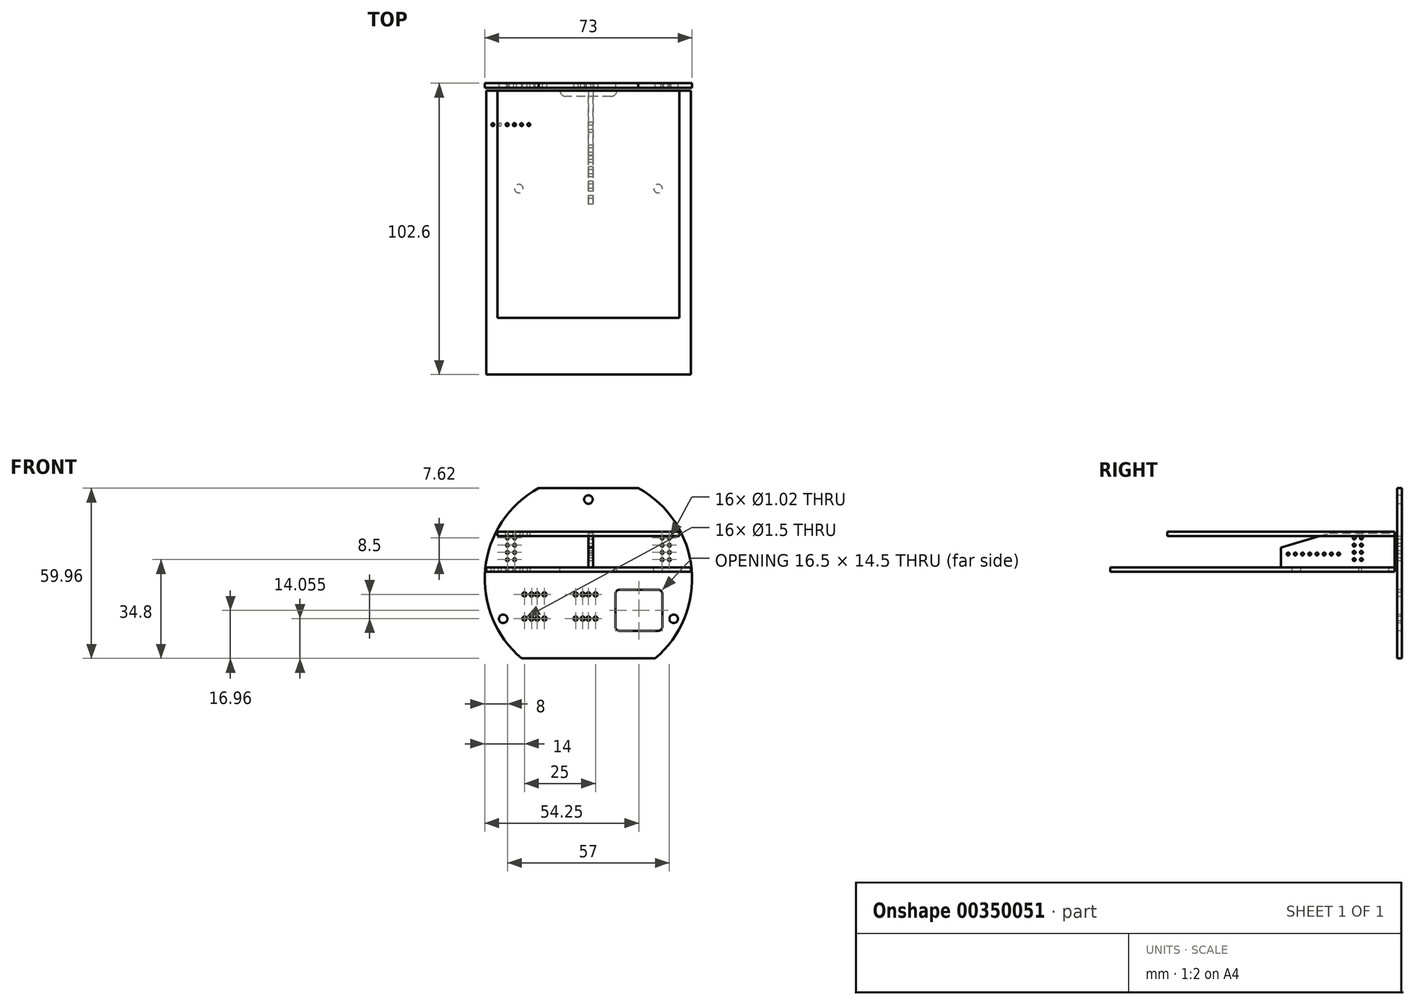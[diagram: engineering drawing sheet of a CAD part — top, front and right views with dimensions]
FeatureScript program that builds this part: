
annotation { "Feature Type Name" : "Feature", "Feature Type Description" : "" }
export const myFeature = defineFeature(function(context is Context, id is Id, definition is map)
    precondition{}
    {
        {
            var Q0;
            Q0=qCreatedBy(makeId("Front.planeOp"),FACE);
            var sketch = newSketch(context, id + "F0", { "sketchPlane" : qUnion([Q0])});
            skCircle(sketch, "E0", {"center": v(0, 0) * mm, "radius": 36.5 * mm});
            skLineSegment(sketch, "E1", {"start": v(-23.46, -27.96) * mm, "end": v(23.46, -27.96) * mm});
            skLineSegment(sketch, "E2", {"start": v(0, 0) * mm, "end": v(-23.46, -27.96) * mm, "construction": true});
            skLineSegment(sketch, "E3", {"start": v(0, 0) * mm, "end": v(23.46, -27.96) * mm, "construction": true});
            skLineSegment(sketch, "E4", {"start": v(17.56, 32) * mm, "end": v(-17.56, 32) * mm});
            skSolve(sketch);
        }
        {
            var Q0;
            {var subQ0=sQuery(id+"F0.wireOp",EDGE,"E1");Q0=makeQuery(id+"F0.imprint","IMPRINT",FACE,{"disambiguationData":[TD([[makeQuery(id+"F0.imprint","IMPRINT",EDGE,{"derivedFrom":subQ0}),1.0]])]});}
            extrude(context, id + "F1", {"entities" : qUnion([Q0]), "depth" : 1.6 * mm});
        }
        {
            var Q0;
            Q0=makeQuery(id+"F1.opExtrude","CAP_FACE",FACE,{"disambiguationData":[OSD([sQuery(id+"F0.wireOp",EDGE,"E0"),sQuery(id+"F0.wireOp",EDGE,"E1")])],"isStart":false});
            var sketch = newSketch(context, id + "F2", { "sketchPlane" : qUnion([Q0])});
            skCircle(sketch, "E5", {"center": v(28.5, 14.46) * mm, "radius": 0.5 * mm});
            skCircle(sketch, "E6.0.1.0", {"center": v(28.5, 11.92) * mm, "radius": 0.5 * mm});
            skCircle(sketch, "E6.0.2.0", {"center": v(28.5, 9.38) * mm, "radius": 0.5 * mm});
            skCircle(sketch, "E6.0.3.0", {"center": v(28.5, 6.84) * mm, "radius": 0.5 * mm});
            skCircle(sketch, "E6.1.0.0", {"center": v(25.96, 14.46) * mm, "radius": 0.5 * mm});
            skCircle(sketch, "E6.1.1.0", {"center": v(25.96, 11.92) * mm, "radius": 0.5 * mm});
            skCircle(sketch, "E6.1.2.0", {"center": v(25.96, 9.38) * mm, "radius": 0.5 * mm});
            skCircle(sketch, "E6.1.3.0", {"center": v(25.96, 6.84) * mm, "radius": 0.5 * mm});
            skLineSegment(sketch, "E6.direction1", {"start": v(28.5, 14.46) * mm, "end": v(25.96, 14.46) * mm, "construction": true});
            skLineSegment(sketch, "E6.direction2", {"start": v(28.5, 14.46) * mm, "end": v(28.5, 11.92) * mm, "construction": true});
            skLineSegment(sketch, "E7.bottom", {"start": v(24.5, -3.75) * mm, "end": v(11, -3.75) * mm});
            skLineSegment(sketch, "E7.top", {"start": v(24.5, -18.25) * mm, "end": v(11, -18.25) * mm});
            skLineSegment(sketch, "E7.left", {"start": v(26, -5.25) * mm, "end": v(26, -16.75) * mm});
            skLineSegment(sketch, "E7.right", {"start": v(9.5, -5.25) * mm, "end": v(9.5, -16.75) * mm});
            skPoint(sketch, "E7.middle", {"position": v(17.75, -11) * mm});
            skPoint(sketch, "E8.visualSharp", {"position": v(9.5, -3.75) * mm});
            skArc(sketch, "E8.filletArc", {"start": v(11, -3.75) * mm, "mid": v(9.94, -4.19) * mm, "end": v(9.5, -5.25) * mm});
            skPoint(sketch, "E9.visualSharp", {"position": v(26, -3.75) * mm});
            skArc(sketch, "E9.filletArc", {"start": v(26, -5.25) * mm, "mid": v(25.56, -4.19) * mm, "end": v(24.5, -3.75) * mm});
            skPoint(sketch, "E10.visualSharp", {"position": v(26, -18.25) * mm});
            skArc(sketch, "E10.filletArc", {"start": v(24.5, -18.25) * mm, "mid": v(25.56, -17.81) * mm, "end": v(26, -16.75) * mm});
            skPoint(sketch, "E11.visualSharp", {"position": v(9.5, -18.25) * mm});
            skArc(sketch, "E11.filletArc", {"start": v(9.5, -16.75) * mm, "mid": v(9.94, -17.81) * mm, "end": v(11, -18.25) * mm});
            skCircle(sketch, "E12", {"center": v(-22.5, -5.4) * mm, "radius": 0.75 * mm});
            skCircle(sketch, "E13", {"center": v(-20, -5.4) * mm, "radius": 0.75 * mm});
            skCircle(sketch, "E14", {"center": v(-18, -5.4) * mm, "radius": 0.75 * mm});
            skCircle(sketch, "E15", {"center": v(-15.5, -5.4) * mm, "radius": 0.75 * mm});
            skCircle(sketch, "E16.0.1.0", {"center": v(-22.5, -13.9) * mm, "radius": 0.75 * mm});
            skCircle(sketch, "E16.0.1.1", {"center": v(-20, -13.9) * mm, "radius": 0.75 * mm});
            skCircle(sketch, "E16.0.1.2", {"center": v(-18, -13.9) * mm, "radius": 0.75 * mm});
            skCircle(sketch, "E16.0.1.3", {"center": v(-15.5, -13.9) * mm, "radius": 0.75 * mm});
            skCircle(sketch, "E16.1.0.0", {"center": v(-4.5, -5.4) * mm, "radius": 0.75 * mm});
            skCircle(sketch, "E16.1.0.1", {"center": v(-2, -5.4) * mm, "radius": 0.75 * mm});
            skCircle(sketch, "E16.1.0.2", {"center": v(0, -5.4) * mm, "radius": 0.75 * mm});
            skCircle(sketch, "E16.1.0.3", {"center": v(2.5, -5.4) * mm, "radius": 0.75 * mm});
            skCircle(sketch, "E16.1.1.0", {"center": v(-4.5, -13.9) * mm, "radius": 0.75 * mm});
            skCircle(sketch, "E16.1.1.1", {"center": v(-2, -13.9) * mm, "radius": 0.75 * mm});
            skCircle(sketch, "E16.1.1.2", {"center": v(0, -13.9) * mm, "radius": 0.75 * mm});
            skCircle(sketch, "E16.1.1.3", {"center": v(2.5, -13.9) * mm, "radius": 0.75 * mm});
            skLineSegment(sketch, "E16.direction1", {"start": v(-22.5, -5.4) * mm, "end": v(-4.5, -5.4) * mm, "construction": true});
            skLineSegment(sketch, "E16.direction2", {"start": v(-22.5, -5.4) * mm, "end": v(-22.5, -13.9) * mm, "construction": true});
            skPoint(sketch, "E17", {"position": v(-36.5, 0) * mm});
            skLineSegment(sketch, "E18", {"start": v(0, 0) * mm, "end": v(0, 16.77) * mm, "construction": true});
            skCircle(sketch, "E19.MirrorC", {"center": v(-25.96, 6.84) * mm, "radius": 0.5 * mm});
            skCircle(sketch, "E20.MirrorC", {"center": v(-25.96, 9.38) * mm, "radius": 0.5 * mm});
            skCircle(sketch, "E21.MirrorC", {"center": v(-25.96, 11.92) * mm, "radius": 0.5 * mm});
            skCircle(sketch, "E22.MirrorC", {"center": v(-25.96, 14.46) * mm, "radius": 0.5 * mm});
            skCircle(sketch, "E23.MirrorC", {"center": v(-28.5, 14.46) * mm, "radius": 0.5 * mm});
            skCircle(sketch, "E24.MirrorC", {"center": v(-28.5, 11.92) * mm, "radius": 0.5 * mm});
            skCircle(sketch, "E25.MirrorC", {"center": v(-28.5, 9.38) * mm, "radius": 0.5 * mm});
            skCircle(sketch, "E26.MirrorC", {"center": v(-28.5, 6.84) * mm, "radius": 0.5 * mm});
            skLineSegment(sketch, "E27", {"start": v(28.5, 6.84) * mm, "end": v(25.96, 14.46) * mm, "construction": true});
            skLineSegment(sketch, "E28.bottom", {"start": v(29.73, 15.98) * mm, "end": v(24.73, 15.98) * mm, "construction": true});
            skLineSegment(sketch, "E28.top", {"start": v(29.73, 5.32) * mm, "end": v(24.73, 5.32) * mm, "construction": true});
            skLineSegment(sketch, "E28.left", {"start": v(29.73, 15.98) * mm, "end": v(29.73, 5.32) * mm, "construction": true});
            skLineSegment(sketch, "E28.right", {"start": v(24.73, 15.98) * mm, "end": v(24.73, 5.32) * mm, "construction": true});
            skPoint(sketch, "E28.middle", {"position": v(27.23, 10.65) * mm});
            skLineSegment(sketch, "E29", {"start": v(31.33, 17.45) * mm, "end": v(31.33, 3.87) * mm, "construction": true});
            skCircle(sketch, "E30", {"center": v(0, 28) * mm, "radius": 1.5 * mm});
            skCircle(sketch, "E31", {"center": v(-30, -14) * mm, "radius": 1.5 * mm});
            skCircle(sketch, "E32.MirrorC", {"center": v(30, -14) * mm, "radius": 1.5 * mm});
            skSolve(sketch);
        }
        {
            var Q0;
            Q0=qSketchRegion(id+"F2",true);
            extrude(context, id + "F3", {"entities" : qUnion([Q0]), "operationType" : NewBodyOperationType.REMOVE, "oppositeDirection" : true, "depth" : 25 * mm});
        }
        {
            var Q0;
            Q0=makeQuery(id+"F1.opExtrude","CAP_FACE",FACE,{"disambiguationData":[OSD([sQuery(id+"F0.wireOp",EDGE,"E0"),sQuery(id+"F0.wireOp",EDGE,"E1")])],"isStart":false});
            cPlane(context, id + "F4", {"entities" : qUnion([Q0]), "cplaneType" : CPlaneType.OFFSET, "offset" : 1 * mm, "width" : 150 * mm, "height" : 150 * mm});
        }
        {
            var Q0;
            Q0=qCreatedBy(id+"F4.planeOp",FACE);
            var sketch = newSketch(context, id + "F5", { "sketchPlane" : qUnion([Q0])});
            skLineSegment(sketch, "E33.bottom", {"start": v(-36, 4.12) * mm, "end": v(36, 4.12) * mm});
            skLineSegment(sketch, "E33.top", {"start": v(-36, 2.52) * mm, "end": v(36, 2.52) * mm});
            skLineSegment(sketch, "E33.left", {"start": v(-36, 4.12) * mm, "end": v(-36, 2.52) * mm});
            skLineSegment(sketch, "E33.right", {"start": v(36, 4.12) * mm, "end": v(36, 2.52) * mm});
            skPoint(sketch, "E33.middle", {"position": v(0, 3.32) * mm});
            skCircle(sketch, "E34", {"center": v(0, 0) * mm, "radius": 36.5 * mm, "construction": true});
            skSolve(sketch);
        }
        {
            var Q0;
            Q0=qSketchRegion(id+"F5",true);
            extrude(context, id + "F6", {"entities" : qUnion([Q0]), "depth" : 100 * mm});
        }
        {
            var Q0;
            Q0=makeQuery(id+"F6.opExtrude","SWEPT_FACE",FACE,{"disambiguationData":[OSD([sQuery(id+"F5.wireOp",EDGE,"E33.bottom")])]});
            var sketch = newSketch(context, id + "F7", { "sketchPlane" : qUnion([Q0])});
            skCircle(sketch, "E35", {"center": v(24.5, -37.1) * mm, "radius": 1.5 * mm});
            skLineSegment(sketch, "E36", {"start": v(0, 0) * mm, "end": v(0, -31.2) * mm, "construction": true});
            skPoint(sketch, "E36.endSnap0", {"position": v(0, -2.6) * mm});
            skPoint(sketch, "E37", {"position": v(0, -102.6) * mm});
            skLineSegment(sketch, "E38.bottom", {"start": v(10, -2.6) * mm, "end": v(-10, -2.6) * mm});
            skLineSegment(sketch, "E38.top", {"start": v(8, -4.6) * mm, "end": v(-8, -4.6) * mm});
            skLineSegment(sketch, "E38.left", {"start": v(10, -2.6) * mm, "end": v(10, -2.6) * mm});
            skLineSegment(sketch, "E38.right", {"start": v(-10, -2.6) * mm, "end": v(-10, -2.6) * mm});
            skPoint(sketch, "E38.middle", {"position": v(0, -3.6) * mm});
            skPoint(sketch, "E39.visualSharp", {"position": v(10, -4.6) * mm});
            skArc(sketch, "E39.filletArc", {"start": v(8, -4.6) * mm, "mid": v(9.41, -4.01) * mm, "end": v(10, -2.6) * mm});
            skPoint(sketch, "E40.visualSharp", {"position": v(-10, -4.6) * mm});
            skArc(sketch, "E40.filletArc", {"start": v(-10, -2.6) * mm, "mid": v(-9.41, -4.01) * mm, "end": v(-8, -4.6) * mm});
            skCircle(sketch, "E41.MirrorC", {"center": v(-24.5, -37.1) * mm, "radius": 1.5 * mm});
            skCircle(sketch, "E42", {"center": v(-26, -14.57) * mm, "radius": 0.5 * mm});
            skCircle(sketch, "E43.1.0.0", {"center": v(-28.54, -14.57) * mm, "radius": 0.5 * mm});
            skCircle(sketch, "E43.2.0.0", {"center": v(-31.08, -14.57) * mm, "radius": 0.5 * mm});
            skCircle(sketch, "E43.3.0.0", {"center": v(-33.62, -14.57) * mm, "radius": 0.5 * mm});
            skLineSegment(sketch, "E43.direction1", {"start": v(-26, -14.57) * mm, "end": v(-28.54, -14.57) * mm, "construction": true});
            skSolve(sketch);
        }
        {
            var Q0;
            Q0=qSketchRegion(id+"F7",true);
            extrude(context, id + "F8", {"entities" : qUnion([Q0]), "operationType" : NewBodyOperationType.REMOVE, "oppositeDirection" : true, "depth" : 25 * mm});
        }
        {
            var Q0;
            Q0=qCreatedBy(makeId("Right.planeOp"),FACE);
            var sketch = newSketch(context, id + "F9", { "sketchPlane" : qUnion([Q0])});
            skLineSegment(sketch, "E44", {"start": v(-2.6, 16.12) * mm, "end": v(-2.6, 4.12) * mm});
            skLineSegment(sketch, "E45", {"start": v(-2.6, 4.12) * mm, "end": v(-42.6, 4.12) * mm});
            skLineSegment(sketch, "E46", {"start": v(-42.6, 4.12) * mm, "end": v(-42.6, 11.12) * mm});
            skLineSegment(sketch, "E47", {"start": v(-42.6, 11.12) * mm, "end": v(-25.6, 16.12) * mm});
            skLineSegment(sketch, "E48", {"start": v(-25.6, 16.12) * mm, "end": v(-2.6, 16.12) * mm});
            skCircle(sketch, "E49", {"center": v(-14.24, 14.46) * mm, "radius": 0.5 * mm});
            skCircle(sketch, "E50.0.1.0", {"center": v(-14.24, 11.92) * mm, "radius": 0.5 * mm});
            skCircle(sketch, "E50.0.2.0", {"center": v(-14.24, 9.38) * mm, "radius": 0.5 * mm});
            skCircle(sketch, "E50.0.3.0", {"center": v(-14.24, 6.84) * mm, "radius": 0.5 * mm});
            skCircle(sketch, "E50.1.0.0", {"center": v(-16.78, 14.46) * mm, "radius": 0.5 * mm});
            skCircle(sketch, "E50.1.1.0", {"center": v(-16.78, 11.92) * mm, "radius": 0.5 * mm});
            skCircle(sketch, "E50.1.2.0", {"center": v(-16.78, 9.38) * mm, "radius": 0.5 * mm});
            skCircle(sketch, "E50.1.3.0", {"center": v(-16.78, 6.84) * mm, "radius": 0.5 * mm});
            skLineSegment(sketch, "E50.direction1", {"start": v(-14.24, 14.46) * mm, "end": v(-16.78, 14.46) * mm, "construction": true});
            skLineSegment(sketch, "E50.direction2", {"start": v(-14.24, 14.46) * mm, "end": v(-14.24, 11.92) * mm, "construction": true});
            skCircle(sketch, "E51", {"center": v(-22.28, 8.8) * mm, "radius": 0.5 * mm});
            skCircle(sketch, "E52.1.0.0", {"center": v(-24.82, 8.8) * mm, "radius": 0.5 * mm});
            skCircle(sketch, "E52.2.0.0", {"center": v(-27.36, 8.8) * mm, "radius": 0.5 * mm});
            skCircle(sketch, "E52.3.0.0", {"center": v(-29.9, 8.8) * mm, "radius": 0.5 * mm});
            skLineSegment(sketch, "E52.direction1", {"start": v(-22.28, 8.8) * mm, "end": v(-24.82, 8.8) * mm, "construction": true});
            skLineSegment(sketch, "E52.direction2", {"start": v(-22.28, 8.8) * mm, "end": v(-22.28, 6.26) * mm, "construction": true});
            skLineSegment(sketch, "E53.0", {"start": v(-1.6, 14.97) * mm, "end": v(-1.6, 13.95) * mm, "construction": true});
            skPoint(sketch, "E54", {"position": v(-1.6, 14.46) * mm});
            skCircle(sketch, "E55.0.4.0", {"center": v(-32.44, 8.8) * mm, "radius": 0.5 * mm});
            skCircle(sketch, "E55.0.5.0", {"center": v(-34.98, 8.8) * mm, "radius": 0.5 * mm});
            skCircle(sketch, "E55.0.6.0", {"center": v(-37.52, 8.8) * mm, "radius": 0.5 * mm});
            skCircle(sketch, "E55.0.7.0", {"center": v(-40.06, 8.8) * mm, "radius": 0.5 * mm});
            skSolve(sketch);
        }
        {
            var Q0;
            Q0=qSketchRegion(id+"F9",true);
            extrude(context, id + "F10", {"entities" : qUnion([Q0]), "depth" : 1.6 * mm});
        }
        {
            var Q0;
            {var subQ0=sQuery(id+"F5.wireOp",EDGE,"E33.bottom");var subQ1=sQuery(id+"F5.wireOp",EDGE,"E33.top");var subQ2=sQuery(id+"F5.wireOp",EDGE,"E33.left");Q0=makeQuery(id+"F8.boolean.opBoolean","SPLIT",FACE,{"disambiguationData":[TD([makeQuery(id+"F6.opExtrude","SWEPT_FACE",FACE,{"disambiguationData":[OSD([subQ2])]})])],"derivedFrom":makeQuery(id+"F6.opExtrude","CAP_FACE",FACE,{"disambiguationData":[OSD([subQ0,subQ1,subQ2,sQuery(id+"F5.wireOp",EDGE,"E33.right")])],"isStart":true})});}
            var sketch = newSketch(context, id + "F11", { "sketchPlane" : qUnion([Q0])});
            skLineSegment(sketch, "E56.bottom", {"start": v(32, 16.72) * mm, "end": v(-32, 16.72) * mm});
            skLineSegment(sketch, "E56.top", {"start": v(32, 15.12) * mm, "end": v(-32, 15.12) * mm});
            skLineSegment(sketch, "E56.left", {"start": v(32, 16.72) * mm, "end": v(32, 15.12) * mm});
            skLineSegment(sketch, "E56.right", {"start": v(-32, 16.72) * mm, "end": v(-32, 15.12) * mm});
            skPoint(sketch, "E56.middle", {"position": v(0, 15.92) * mm});
            skSolve(sketch);
        }
        {
            var Q0;
            Q0=qSketchRegion(id+"F11",true);
            extrude(context, id + "F12", {"entities" : qUnion([Q0]), "oppositeDirection" : true, "depth" : 80 * mm});
        }
        {
            var Q0;
            Q0=makeQuery(id+"F12.opExtrude","SWEPT_FACE",FACE,{"disambiguationData":[OSD([sQuery(id+"F11.wireOp",EDGE,"E56.bottom")])]});
            var sketch = newSketch(context, id + "F13", { "sketchPlane" : qUnion([Q0])});
            skCircle(sketch, "E57", {"center": v(-21, -14.57) * mm, "radius": 0.5 * mm});
            skCircle(sketch, "E58.1.0.0", {"center": v(-23.54, -14.57) * mm, "radius": 0.5 * mm});
            skCircle(sketch, "E58.2.0.0", {"center": v(-26.08, -14.57) * mm, "radius": 0.5 * mm});
            skCircle(sketch, "E58.3.0.0", {"center": v(-28.62, -14.57) * mm, "radius": 0.5 * mm});
            skLineSegment(sketch, "E58.direction1", {"start": v(-21, -14.57) * mm, "end": v(-23.54, -14.57) * mm, "construction": true});
            skSolve(sketch);
        }
        {
            var Q0;
            Q0=qSketchRegion(id+"F13",true);
            extrude(context, id + "F14", {"entities" : qUnion([Q0]), "operationType" : NewBodyOperationType.REMOVE, "oppositeDirection" : true, "depth" : 25 * mm});
        }
    });
